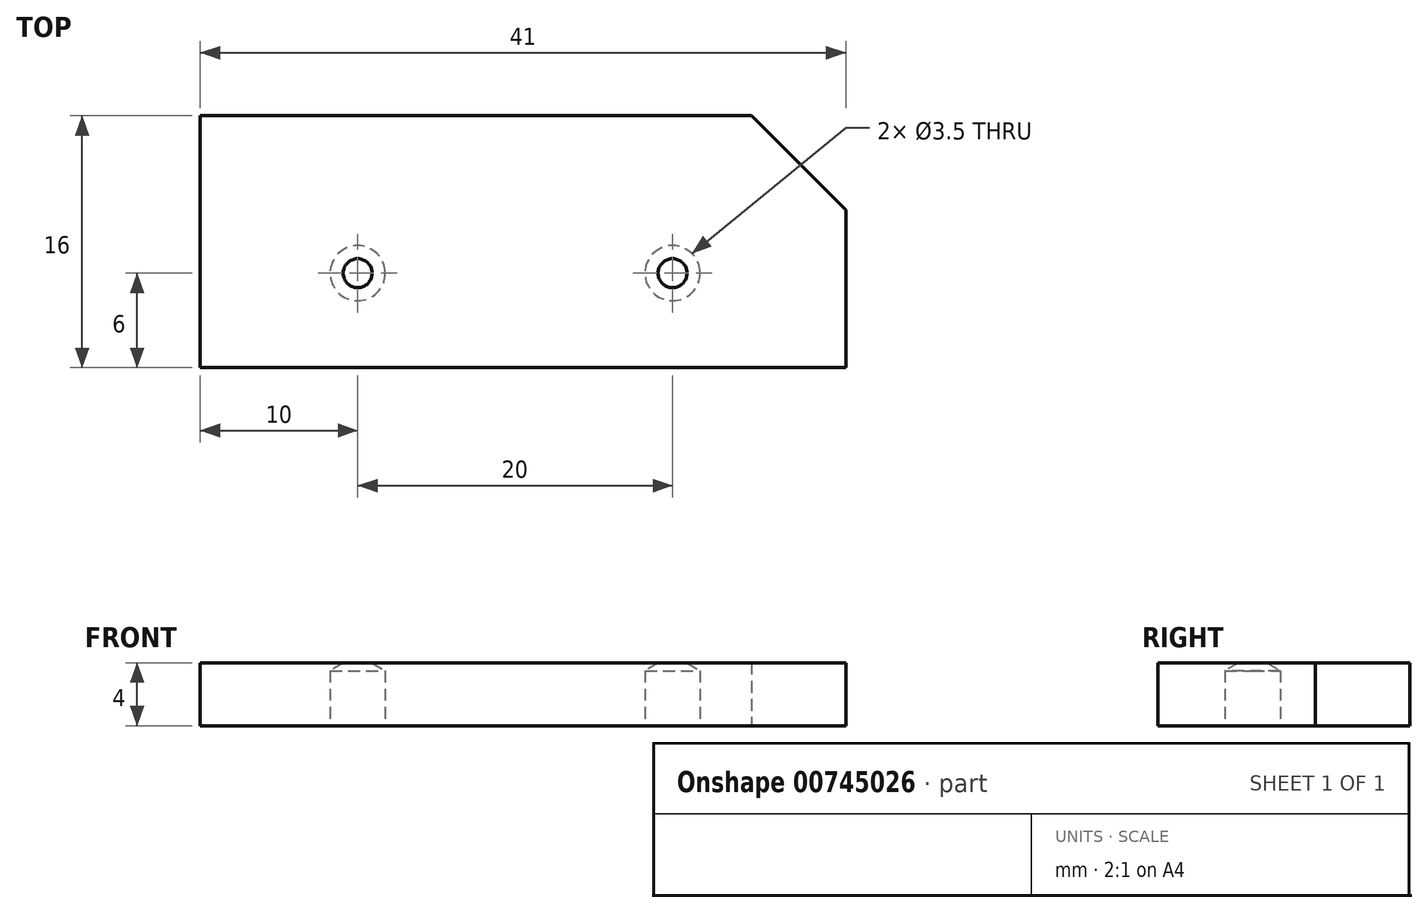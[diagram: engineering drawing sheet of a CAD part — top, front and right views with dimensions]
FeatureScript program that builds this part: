
annotation { "Feature Type Name" : "Feature", "Feature Type Description" : "" }
export const myFeature = defineFeature(function(context is Context, id is Id, definition is map)
    precondition{}
    {
        {
            var Q0;
            Q0=qCreatedBy(makeId("Top.planeOp"),FACE);
            var sketch = newSketch(context, id + "F0", { "sketchPlane" : qUnion([Q0])});
            skLineSegment(sketch, "E0.bottom", {"start": v(20.5, -8) * mm, "end": v(-20.5, -8) * mm});
            skLineSegment(sketch, "E0.top", {"start": v(20.5, 8) * mm, "end": v(-20.5, 8) * mm});
            skLineSegment(sketch, "E0.left", {"start": v(20.5, -8) * mm, "end": v(20.5, 8) * mm});
            skLineSegment(sketch, "E0.right", {"start": v(-20.5, -8) * mm, "end": v(-20.5, 8) * mm});
            skPoint(sketch, "E0.middle", {"position": v(0, 0) * mm});
            skPoint(sketch, "E1", {"position": v(-10.5, -2) * mm});
            skPoint(sketch, "E2", {"position": v(9.5, -2) * mm});
            skSolve(sketch);
        }
        {
            var Q0;
            Q0=makeQuery(id+"F0.imprint","IMPRINT",FACE,{"disambiguationData":[TD([[makeQuery(id+"F0.imprint","IMPRINT",EDGE,{"derivedFrom":sQuery(id+"F0.wireOp",EDGE,"E0.bottom")}),-1.0]])]});
            extrude(context, id + "F1", {"entities" : qUnion([Q0]), "depth" : 4 * mm, "offsetDistance" : 25 * mm});
        }
        {
            var Q0;
            Q0=sQuery(id+"F0.wireOp",VERTEX,"E1");
            var Q1;
            Q1=sQuery(id+"F0.wireOp",VERTEX,"E2");
            var Q2;
            Q2=makeQuery(id+"F1.opExtrude","SWEPT_BODY",BODY,{"disambiguationData":[OSD([sQuery(id+"F0.wireOp",EDGE,"E0.bottom"),sQuery(id+"F0.wireOp",EDGE,"E0.top"),sQuery(id+"F0.wireOp",EDGE,"E0.left"),sQuery(id+"F0.wireOp",EDGE,"E0.right")])]});
            hole(context, id + "F2", {"style" : HoleStyle.SIMPLE, "endStyle" : HoleEndStyle.BLIND, "oppositeDirection" : true, "holeDiameter" : 3.5 * mm, "majorDiameter" : 5 * mm, "holeDepth" : 3.5 * mm, "isTappedThrough" : true, "tappedDepth" : 6 * mm, "tapClearance" : 3, "locations" : qUnion([Q0, Q1]), "scope" : qUnion([Q2])});
        }
        {
            var Q0;
            Q0=makeQuery(id+"F1.opExtrude","SWEPT_EDGE",EDGE,{"disambiguationData":[OSD([sQuery(id+"F0.wireOp",EDGE,"E0.top"),sQuery(id+"F0.wireOp",EDGE,"E0.left")])]});
            chamfer(context, id + "F3", {"entities" : qUnion([Q0]), "width" : 6 * mm, "tangentPropagation" : true});
        }
    });
